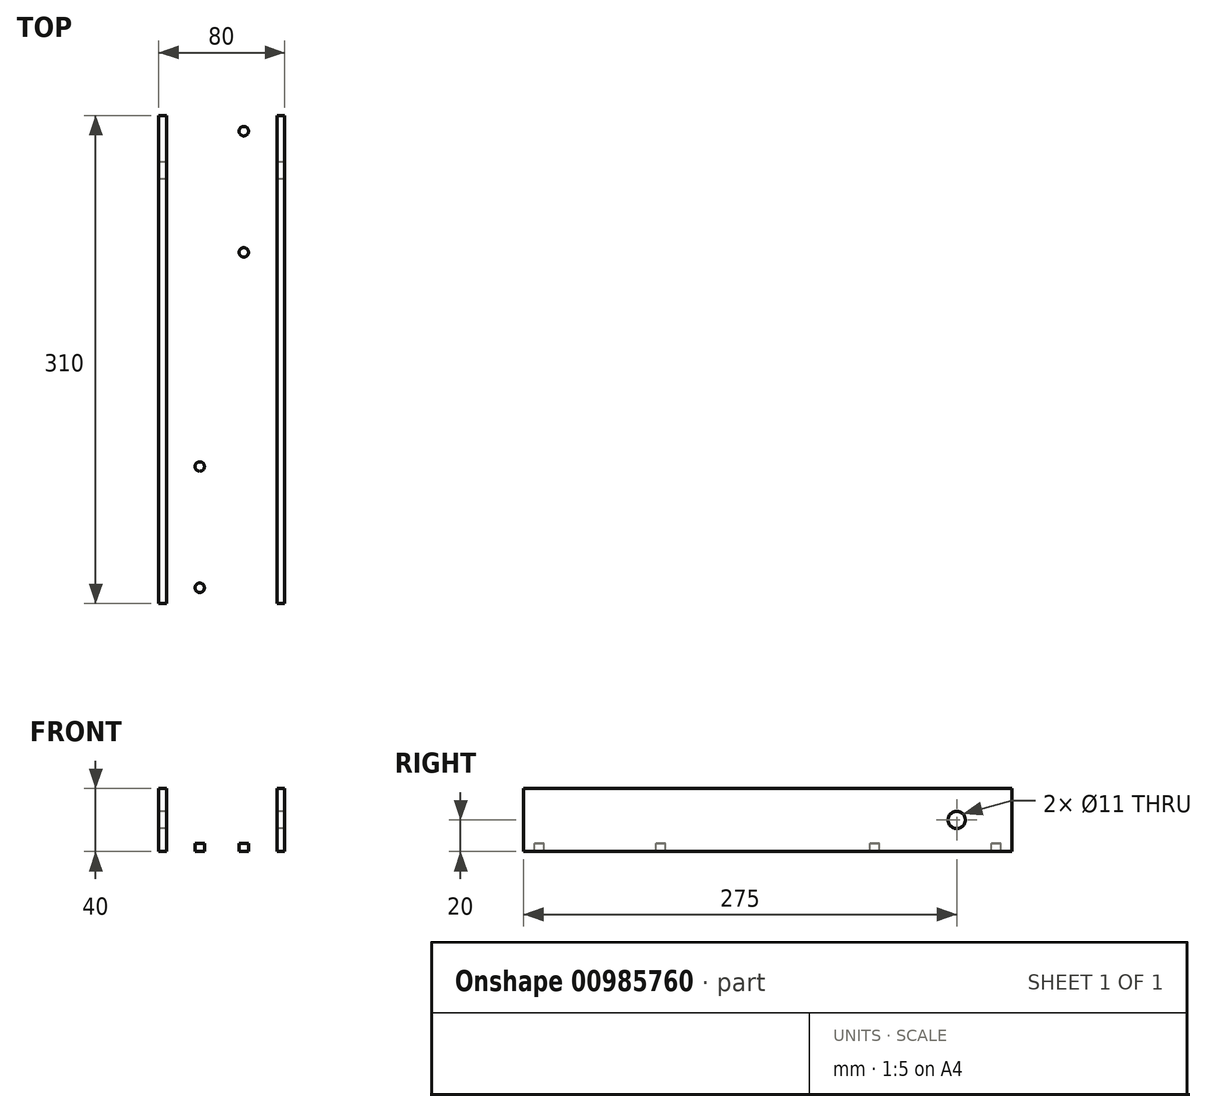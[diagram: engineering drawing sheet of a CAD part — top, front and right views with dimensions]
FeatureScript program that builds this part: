
annotation { "Feature Type Name" : "Feature", "Feature Type Description" : "" }
export const myFeature = defineFeature(function(context is Context, id is Id, definition is map)
    precondition{}
    {
        {
            var Q0;
            Q0=qCreatedBy(makeId("Front.planeOp"),FACE);
            var sketch = newSketch(context, id + "F0", { "sketchPlane" : qUnion([Q0])});
            skLineSegment(sketch, "E0.top", {"start": v(35, -17.5) * mm, "end": v(-35, -17.5) * mm});
            skLineSegment(sketch, "E0.left", {"start": v(35, 17.5) * mm, "end": v(35, -17.5) * mm});
            skLineSegment(sketch, "E0.right", {"start": v(-35, 17.5) * mm, "end": v(-35, -17.5) * mm});
            skPoint(sketch, "E0.middle", {"position": v(0, 0) * mm});
            skLineSegment(sketch, "E1.0", {"start": v(40, 17.5) * mm, "end": v(40, -22.5) * mm});
            skLineSegment(sketch, "E1.1", {"start": v(40, -22.5) * mm, "end": v(-40, -22.5) * mm});
            skLineSegment(sketch, "E1.2", {"start": v(-40, 17.5) * mm, "end": v(-40, -22.5) * mm});
            skLineSegment(sketch, "E2", {"start": v(-35, 17.5) * mm, "end": v(-40, 17.5) * mm});
            skLineSegment(sketch, "E3", {"start": v(35, 17.5) * mm, "end": v(40, 17.5) * mm});
            skSolve(sketch);
        }
        {
            var Q0;
            Q0=makeQuery(id+"F0.imprint","IMPRINT",FACE,{"disambiguationData":[TD([[makeQuery(id+"F0.imprint","IMPRINT",EDGE,{"derivedFrom":sQuery(id+"F0.wireOp",EDGE,"E0.top")}),1.0]])]});
            extrude(context, id + "F1", {"entities" : qUnion([Q0]), "endBound" : BoundingType.SYMMETRIC, "depth" : 310 * mm, "offsetDistance" : 25 * mm});
        }
        {
            var Q0;
            Q0=qCreatedBy(makeId("Right.planeOp"),FACE);
            var sketch = newSketch(context, id + "F2", { "sketchPlane" : qUnion([Q0])});
            skCircle(sketch, "E4", {"center": v(120, -2.5) * mm, "radius": 5.5 * mm});
            skCircle(sketch, "E5.MirrorC", {"center": v(-120, -2.5) * mm, "radius": 5.5 * mm});
            skSolve(sketch);
        }
        {
            var Q0;
            Q0=makeQuery(id+"F2.imprint","IMPRINT",FACE,{"disambiguationData":[TD([[makeQuery(id+"F2.imprint","IMPRINT",EDGE,{"derivedFrom":sQuery(id+"F2.wireOp",EDGE,"E4")}),1.0]])]});
            var Q1;
            Q1=makeQuery(id+"F2.imprint","IMPRINT",FACE,{"disambiguationData":[TD([[makeQuery(id+"F2.imprint","IMPRINT",EDGE,{"derivedFrom":sQuery(id+"F2.wireOp",EDGE,"E5.MirrorC")}),-1.0]])]});
            extrude(context, id + "F3", {"entities" : qUnion([Q0, Q1]), "operationType" : NewBodyOperationType.REMOVE, "endBound" : BoundingType.SYMMETRIC, "depth" : 100 * mm, "offsetDistance" : 25 * mm});
        }
        {
            var Q0;
            Q0=makeQuery(id+"F1.opExtrude","SWEPT_FACE",FACE,{"disambiguationData":[OSD([sQuery(id+"F0.wireOp",EDGE,"E0.top")])]});
            var sketch = newSketch(context, id + "F4", { "sketchPlane" : qUnion([Q0])});
            skCircle(sketch, "E6", {"center": v(-14, 145) * mm, "radius": 3 * mm});
            skCircle(sketch, "E7.MirrorC", {"center": v(14, 145) * mm, "radius": 3 * mm});
            skCircle(sketch, "E8.0.1.0", {"center": v(14, 68) * mm, "radius": 3 * mm});
            skCircle(sketch, "E8.0.1.1", {"center": v(-14, 68) * mm, "radius": 3 * mm});
            skLineSegment(sketch, "E8.direction1", {"start": v(14, 145) * mm, "end": v(65.3, 145) * mm, "construction": true});
            skLineSegment(sketch, "E8.direction2", {"start": v(14, 145) * mm, "end": v(14, 68) * mm, "construction": true});
            skCircle(sketch, "E9.MirrorC", {"center": v(-14, -68) * mm, "radius": 3 * mm});
            skCircle(sketch, "E10.MirrorC", {"center": v(-14, -145) * mm, "radius": 3 * mm});
            skCircle(sketch, "E11.MirrorC", {"center": v(14, -145) * mm, "radius": 3 * mm});
            skCircle(sketch, "E12.MirrorC", {"center": v(14, -68) * mm, "radius": 3 * mm});
            skSolve(sketch);
        }
        {
            var Q0;
            Q0=makeQuery(id+"F4.imprint","IMPRINT",FACE,{"disambiguationData":[TD([[makeQuery(id+"F4.imprint","IMPRINT",EDGE,{"derivedFrom":sQuery(id+"F4.wireOp",EDGE,"E6")}),1.0]])]});
            var Q1;
            Q1=makeQuery(id+"F4.imprint","IMPRINT",FACE,{"disambiguationData":[TD([[makeQuery(id+"F4.imprint","IMPRINT",EDGE,{"derivedFrom":sQuery(id+"F4.wireOp",EDGE,"E7.MirrorC")}),-1.0]])]});
            var Q2;
            Q2=makeQuery(id+"F4.imprint","IMPRINT",FACE,{"disambiguationData":[TD([[makeQuery(id+"F4.imprint","IMPRINT",EDGE,{"derivedFrom":sQuery(id+"F4.wireOp",EDGE,"E8.0.1.1")}),1.0]])]});
            var Q3;
            Q3=makeQuery(id+"F4.imprint","IMPRINT",FACE,{"disambiguationData":[TD([[makeQuery(id+"F4.imprint","IMPRINT",EDGE,{"derivedFrom":sQuery(id+"F4.wireOp",EDGE,"E8.0.1.0")}),-1.0]])]});
            var Q4;
            Q4=makeQuery(id+"F4.imprint","IMPRINT",FACE,{"disambiguationData":[TD([[makeQuery(id+"F4.imprint","IMPRINT",EDGE,{"derivedFrom":sQuery(id+"F4.wireOp",EDGE,"E9.MirrorC")}),-1.0]])]});
            var Q5;
            Q5=makeQuery(id+"F4.imprint","IMPRINT",FACE,{"disambiguationData":[TD([[makeQuery(id+"F4.imprint","IMPRINT",EDGE,{"derivedFrom":sQuery(id+"F4.wireOp",EDGE,"E12.MirrorC")}),1.0]])]});
            var Q6;
            Q6=makeQuery(id+"F4.imprint","IMPRINT",FACE,{"disambiguationData":[TD([[makeQuery(id+"F4.imprint","IMPRINT",EDGE,{"derivedFrom":sQuery(id+"F4.wireOp",EDGE,"E10.MirrorC")}),-1.0]])]});
            var Q7;
            Q7=makeQuery(id+"F4.imprint","IMPRINT",FACE,{"disambiguationData":[TD([[makeQuery(id+"F4.imprint","IMPRINT",EDGE,{"derivedFrom":sQuery(id+"F4.wireOp",EDGE,"E11.MirrorC")}),1.0]])]});
            extrude(context, id + "F5", {"entities" : qUnion([Q0, Q1, Q2, Q3, Q4, Q5, Q6, Q7]), "operationType" : NewBodyOperationType.REMOVE, "oppositeDirection" : true, "depth" : 25 * mm, "offsetDistance" : 25 * mm});
        }
    });
